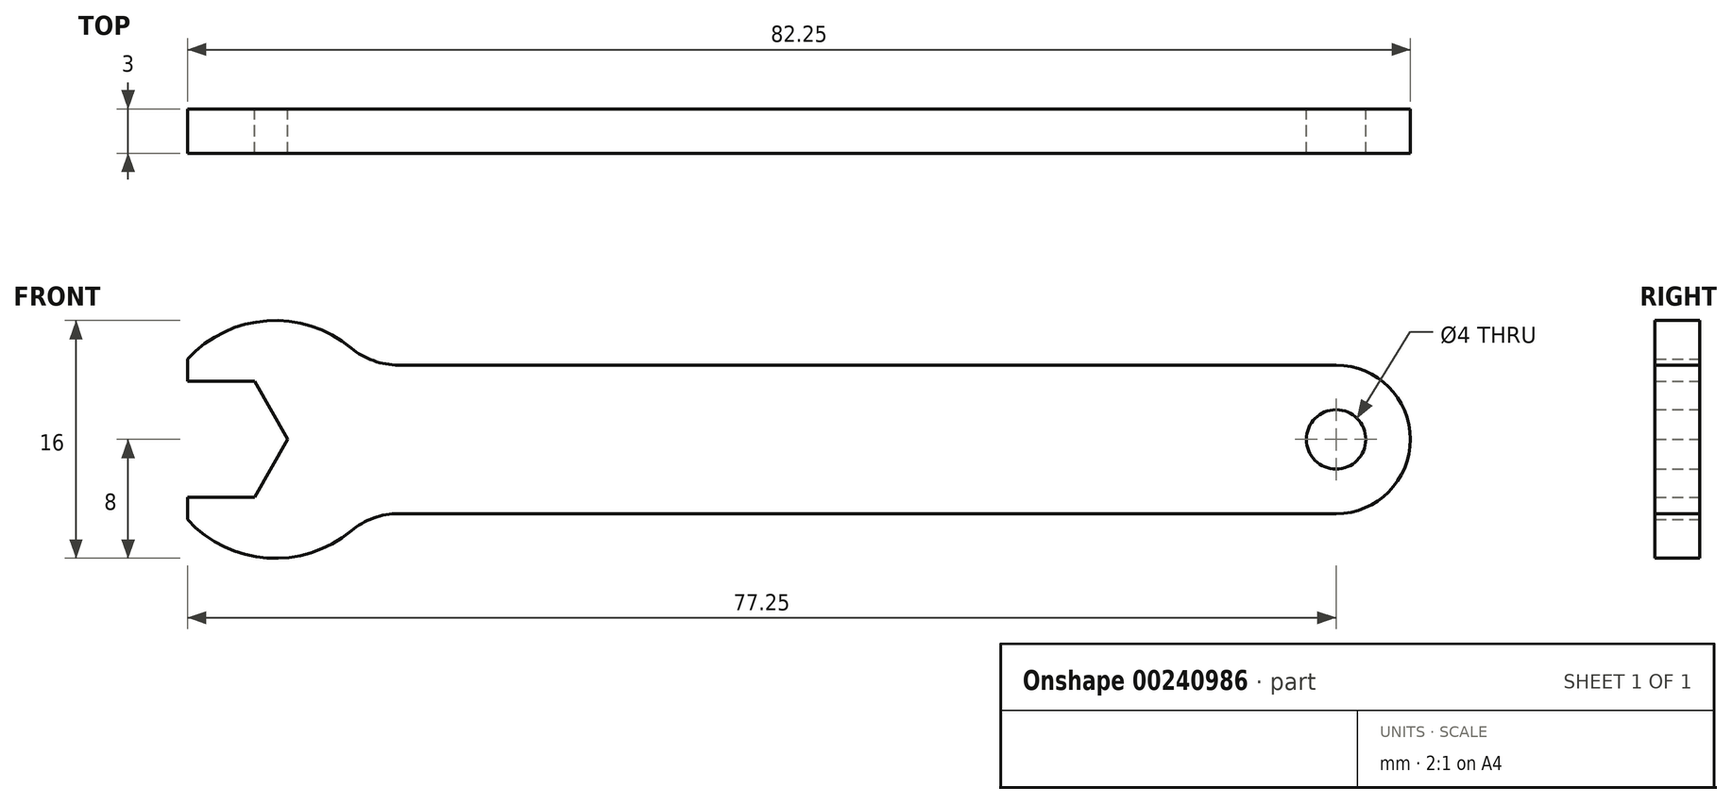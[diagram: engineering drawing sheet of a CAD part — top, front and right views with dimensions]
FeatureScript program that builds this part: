
annotation { "Feature Type Name" : "Feature", "Feature Type Description" : "" }
export const myFeature = defineFeature(function(context is Context, id is Id, definition is map)
    precondition{}
    {
        {
            var Q0;
            Q0=qCreatedBy(makeId("Front.planeOp"),FACE);
            var sketch = newSketch(context, id + "F0", { "sketchPlane" : qUnion([Q0])});
            skCircle(sketch, "E0.cCircle", {"center": v(0, 0) * mm, "radius": 3.9 * mm, "construction": true});
            skLineSegment(sketch, "E0.0", {"start": v(2.25, -3.9) * mm, "end": v(-2.25, -3.9) * mm});
            skLineSegment(sketch, "E0.3", {"start": v(-2.25, 3.9) * mm, "end": v(2.25, 3.9) * mm});
            skLineSegment(sketch, "E0.4", {"start": v(2.25, 3.9) * mm, "end": v(4.5, 0) * mm});
            skLineSegment(sketch, "E0.5", {"start": v(4.5, 0) * mm, "end": v(2.25, -3.9) * mm});
            skPoint(sketch, "E0.0.midPoint", {"position": v(0, -3.9) * mm});
            skLineSegment(sketch, "E1", {"start": v(-2.25, 3.9) * mm, "end": v(-2.25, 5.4) * mm});
            skLineSegment(sketch, "E2.MirrorCS", {"start": v(-2.25, -3.9) * mm, "end": v(-2.25, -5.4) * mm});
            skArc(sketch, "E3", {"start": v(-2.25, -5.4) * mm, "mid": v(3.1, -7.98) * mm, "end": v(8.76, -6.15) * mm});
            skArc(sketch, "E4", {"start": v(75, -5) * mm, "mid": v(80, 0) * mm, "end": v(75, 5) * mm});
            skLineSegment(sketch, "E5", {"start": v(75, 5) * mm, "end": v(11.96, 5) * mm});
            skLineSegment(sketch, "E6.MirrorCS", {"start": v(75, -5) * mm, "end": v(11.96, -5) * mm});
            skArc(sketch, "E7.trimOffspring", {"start": v(8.76, 6.15) * mm, "mid": v(3.1, 7.98) * mm, "end": v(-2.25, 5.4) * mm});
            skPoint(sketch, "E8.visualSharp", {"position": v(9.9, 5) * mm});
            skArc(sketch, "E8.filletArc", {"start": v(8.76, 6.15) * mm, "mid": v(10.26, 5.3) * mm, "end": v(11.96, 5) * mm});
            skPoint(sketch, "E9.visualSharp", {"position": v(9.9, -5) * mm});
            skArc(sketch, "E9.filletArc", {"start": v(11.96, -5) * mm, "mid": v(10.26, -5.3) * mm, "end": v(8.76, -6.15) * mm});
            skPoint(sketch, "E10.orphan", {"position": v(-4.5, 0) * mm});
            skCircle(sketch, "E11", {"center": v(75, 0) * mm, "radius": 2 * mm});
            skSolve(sketch);
        }
        {
            var Q0;
            Q0=makeQuery(id+"F0.imprint","IMPRINT",FACE,{"disambiguationData":[TD([[makeQuery(id+"F0.imprint","IMPRINT",EDGE,{"derivedFrom":sQuery(id+"F0.wireOp",EDGE,"E0.0")}),1.0]])]});
            extrude(context, id + "F1", {"entities" : qUnion([Q0]), "depth" : 3 * mm});
        }
    });
